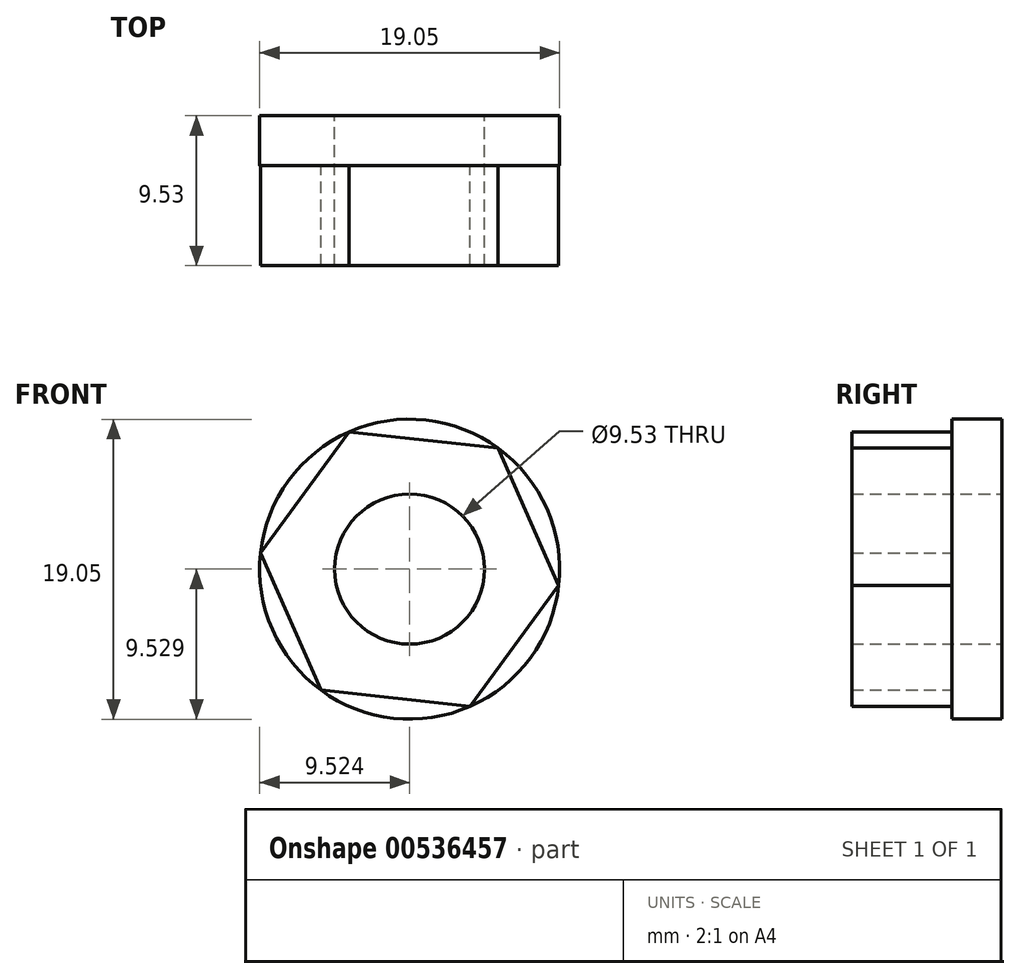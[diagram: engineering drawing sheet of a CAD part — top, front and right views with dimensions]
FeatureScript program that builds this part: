
annotation { "Feature Type Name" : "Feature", "Feature Type Description" : "" }
export const myFeature = defineFeature(function(context is Context, id is Id, definition is map)
    precondition{}
    {
        {
            var Q0;
            Q0=qCreatedBy(makeId("Front.planeOp"),FACE);
            var sketch = newSketch(context, id + "F0", { "sketchPlane" : qUnion([Q0])});
            skCircle(sketch, "E0", {"center": v(-49.28, 2.03) * mm, "radius": 4.76 * mm});
            skCircle(sketch, "E1.0", {"center": v(-49.28, 2.03) * mm, "radius": 9.52 * mm});
            skSolve(sketch);
        }
        {
            var Q0;
            Q0=qSketchRegion(id+"F0",true);
            extrude(context, id + "F1", {"entities" : qUnion([Q0]), "depth" : 3.17 * mm, "offsetDistance" : 25.4 * mm});
        }
        {
            var Q0;
            Q0=makeQuery(id+"F1.opExtrude","CAP_FACE",FACE,{"disambiguationData":[OSD([sQuery(id+"F0.wireOp",EDGE,"E0"),sQuery(id+"F0.wireOp",EDGE,"E1.0")])],"isStart":false});
            var sketch = newSketch(context, id + "F2", { "sketchPlane" : qUnion([Q0])});
            skCircle(sketch, "E2.cCircle", {"center": v(-49.28, 2.03) * mm, "radius": 9.52 * mm});
            skLineSegment(sketch, "E2.0", {"start": v(-39.8, 1) * mm, "end": v(-45.44, -6.69) * mm});
            skLineSegment(sketch, "E2.1", {"start": v(-45.44, -6.69) * mm, "end": v(-54.9, -5.65) * mm});
            skLineSegment(sketch, "E2.2", {"start": v(-54.9, -5.65) * mm, "end": v(-58.74, 3.06) * mm});
            skLineSegment(sketch, "E2.3", {"start": v(-58.74, 3.06) * mm, "end": v(-53.12, 10.75) * mm});
            skLineSegment(sketch, "E2.4", {"start": v(-53.12, 10.75) * mm, "end": v(-43.65, 9.71) * mm});
            skLineSegment(sketch, "E2.5", {"start": v(-43.65, 9.71) * mm, "end": v(-39.8, 1) * mm});
            skSolve(sketch);
        }
        {
            var Q0;
            Q0=makeQuery(id+"F2.imprint","IMPRINT",FACE,{"disambiguationData":[TD([[makeQuery(id+"F2.imprint","IMPRINT",EDGE,{"derivedFrom":sQuery(id+"F2.wireOp",EDGE,"WVDNoywF-x0x1-5jWb-Bc2Q-NXrycg8dcBTV")}),1.0]])]});
            var Q1;
            Q1=makeQuery(id+"F2.imprint","IMPRINT",FACE,{"disambiguationData":[TD([[makeQuery(id+"F2.imprint","IMPRINT",EDGE,{"derivedFrom":sQuery(id+"F2.wireOp",EDGE,"E2.0")}),-1.0]])]});
            extrude(context, id + "F3", {"entities" : qUnion([Q0, Q1]), "operationType" : NewBodyOperationType.ADD, "depth" : 6.35 * mm, "offsetDistance" : 25.4 * mm});
        }
    });
